# Revit family: ГРЕЕРС ЗВП-М3-150Н
name_source: partatom
category: Оборудование
units: mm (PartAtom-declared; Revit-internal decimal feet)

## family parameters
Всегда вертикально = Да
Заголовок OmniClass = Climate Control (HVAC)
На основе рабочей плоскости = Нет
Номер OmniClass = 23.75.00.00
Общий = Нет
При загрузке вырезать с полостями = Нет
Размер круглого соединителя = Использовать диаметр
Тип детали = Нормальный
Точка расчета площади = Нет

## types (1)
- ГРЕЕРС ЗВП-М3-150Н
    URL = https://greers.ru
    Вентилятор = Осевой, однофазный, переменного тока, с 3-х скоростным двигателем, 2 шт.
    Вес аппарата = 58.00 кг
    Группа модели = Воздушная завеса ЗВП-М3-150Н
    Изготовитель = ООО "ЮНИО-ВЕНТ"
    Класс защиты = IP 54
    Классификация нагрузки = Двигатель
    Коэффициент мощности = 1
    Максимальное потребление тока = 0 А
    Материал вентилятора = Пластик
    Материал завесы = Нержавеющая сталь
    Напряжение питания = 230 В
    Описание = Промышленная воздушная завеса без нагрева
    Отметка по умолчанию = 0 мм
    Полная установленная мощность = 0 В·А
    Производительность = 0.0 м³/ч
    Стоимость = 81195 $
